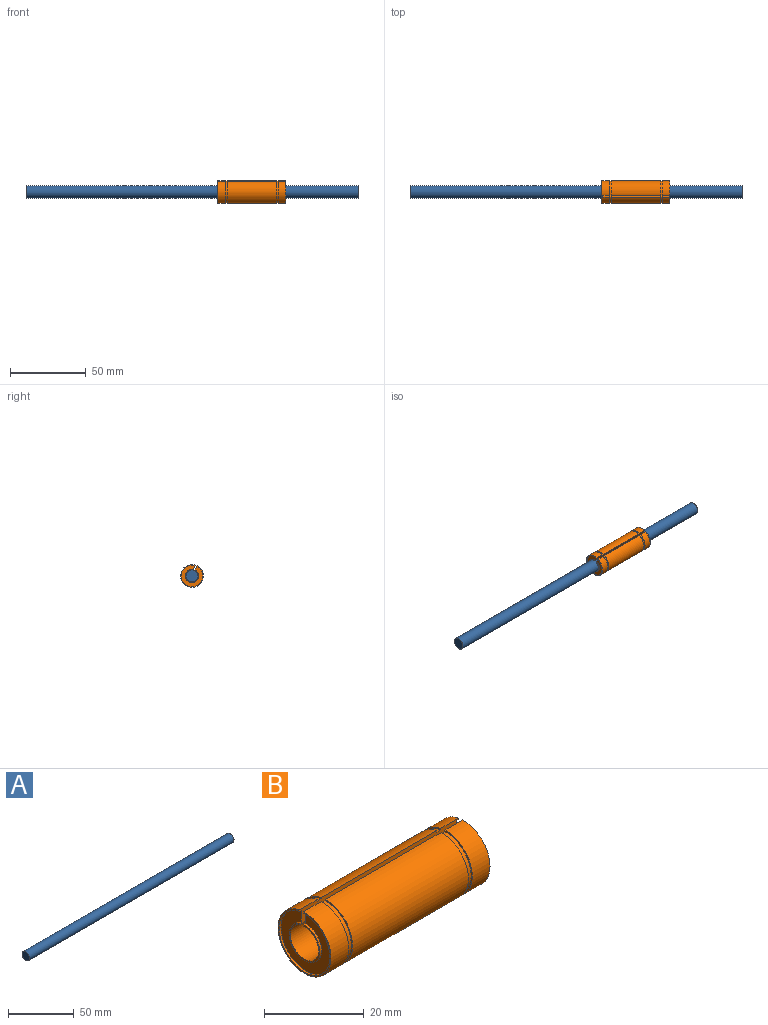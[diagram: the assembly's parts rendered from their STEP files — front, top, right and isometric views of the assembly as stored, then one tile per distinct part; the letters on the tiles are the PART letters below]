
ASSEMBLY  parts=2 mates=1
PART A: 3 faces, bbox 219.5x8x8 mm
  f0: cylinder r=4mm len=219.5mm, axis (-1,0,0), area 5516.6mm2, adj f1,f2
  f1: plane 8x8mm, normal (1,0,0), area 50.3mm2, adj f0
  f2: plane 8x8mm, normal (-1,0,0), area 50.3mm2, adj f0
PART B: 22 faces, bbox 45x15x15 mm
  f0: plane 8.7x8.7mm, normal (-1,0,0), area 8.8mm2, adj f4,f17,f20,f21
  f1: plane 8.7x8.7mm, normal (1,0,0), area 8.8mm2, adj f4,f14,f20,f21
  f2: cylinder r=7.5mm len=32.8mm, axis (-1,0,0), area 1507.4mm2, adj f8,f11,f20,f21
  f3: cylinder r=7.5mm len=15mm, axis (-1,0,0), area 229.8mm2, adj f7,f9,f20,f21
  f4: cylinder r=4mm len=45mm, axis (-1,0,0), area 1077.5mm2, adj f0,f1,f20,f21
  f5: cylinder r=7.5mm len=15mm, axis (-1,0,0), area 229.8mm2, adj f6,f12,f20,f21
  f6: plane 15x15mm, normal (1,0,0), area 15.7mm2, adj f5,f15,f20,f21
  f7: plane 15x15mm, normal (-1,0,0), area 15.7mm2, adj f3,f18,f20,f21
  f8: plane 15x15mm, normal (-1,0,0), area 15.7mm2, adj f2,f10,f20,f21
  f9: plane 15x15mm, normal (1,0,0), area 15.7mm2, adj f3,f10,f20,f21
  f10: cylinder r=7.15mm len=14.3mm, axis (-1,0,0), area 48.1mm2, adj f8,f9,f20,f21
  f11: plane 15x15mm, normal (1,0,0), area 15.7mm2, adj f2,f13,f20,f21
  f12: plane 15x15mm, normal (-1,0,0), area 15.7mm2, adj f5,f13,f20,f21
  f13: cylinder r=7.15mm len=14.3mm, axis (1,0,0), area 48.1mm2, adj f11,f12,f20,f21
  f14: cylinder r=4.35mm len=8.7mm, axis (1,0,0), area 13.1mm2, adj f1,f16,f20,f21
  f15: cylinder r=7.15mm len=14.3mm, axis (1,0,0), area 21.9mm2, adj f6,f16,f20,f21
  f16: plane 14.3x14.3mm, normal (1,0,0), area 97.9mm2, adj f14,f15,f20,f21
  f17: cylinder r=4.35mm len=8.7mm, axis (-1,0,0), area 13.1mm2, adj f0,f19,f20,f21
  f18: cylinder r=7.15mm len=14.3mm, axis (-1,0,0), area 21.9mm2, adj f7,f19,f20,f21
  f19: plane 14.3x14.3mm, normal (-1,0,0), area 97.9mm2, adj f17,f18,f20,f21
  f20: plane 45x3.62mm, normal (0,-1,0), area 159.4mm2, adj f0,f1,f2,f3,f4,f5,f6,f7
  f21: plane 45x3.5mm, normal (0,1,0), area 154.1mm2, adj f0,f1,f2,f3,f4,f5,f6,f7
PLACE A t=(-30.3,-31.85,13.09)mm fixed
PLACE B rot(axis=(1,0,0),28.9deg) t=(9.24,-31.85,13.09)mm
MATE cylindrical B.f4 <-> A.f0  axis (-1,0,0) through (31.74,-31.85,13.09)mm
